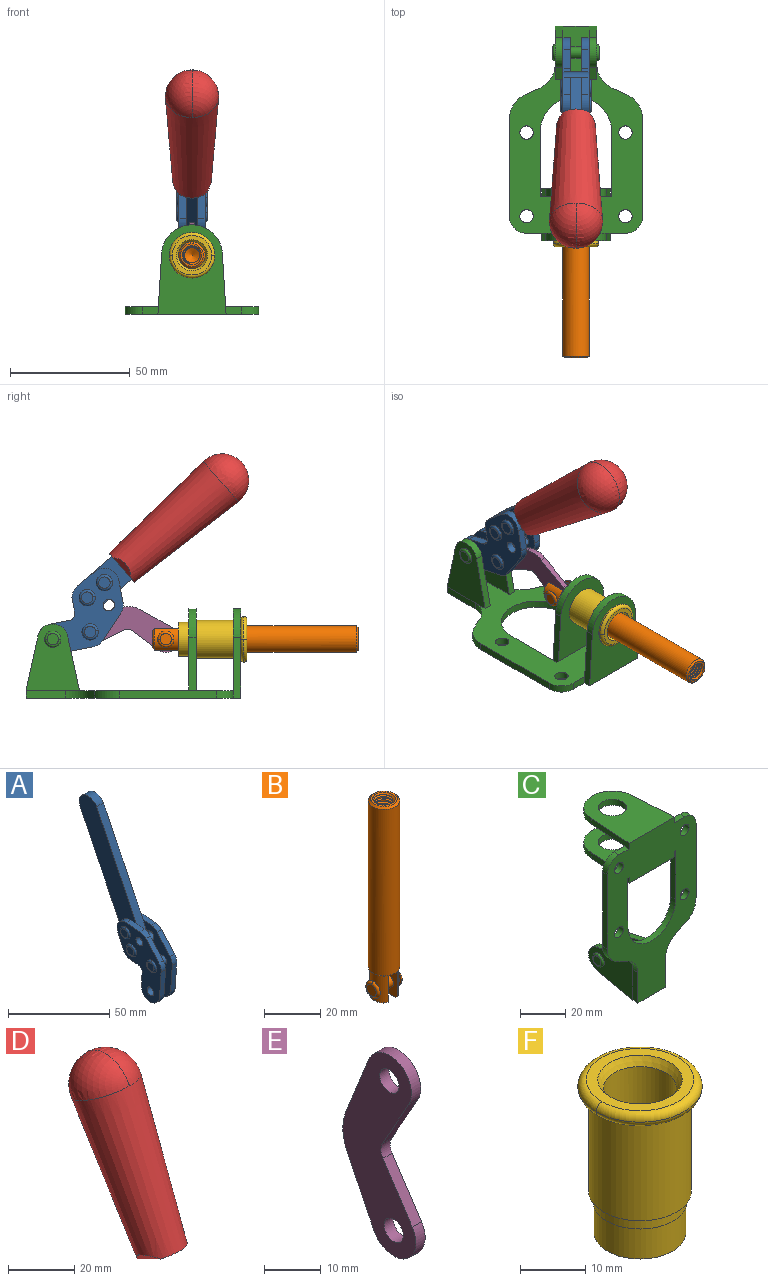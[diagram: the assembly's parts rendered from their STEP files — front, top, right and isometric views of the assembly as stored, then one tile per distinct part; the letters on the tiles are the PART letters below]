
ASSEMBLY  parts=6 mates=6
PART A: 59 faces, bbox 12.9x60.2x99.6 mm
  f0: torus R=2.39mm, axis (-1,0,0), area 14.9mm2, adj f20,f43,f51
  f1: torus R=2.39mm, axis (-1,0,0), area 14.9mm2, adj f19,f42,f51
  f2: torus R=2.39mm, axis (-1,0,0), area 14.9mm2, adj f18,f35,f51
  f3: torus R=2.39mm, axis (-1,0,0), area 14.9mm2, adj f14,f17,f23
  f4: torus R=2.39mm, axis (-1,0,0), area 14.9mm2, adj f13,f16,f23
  f5: torus R=2.39mm, axis (-1,0,0), area 14.9mm2, adj f12,f15,f23
  f6: cylinder r=2.39mm len=4.78mm, axis (1,0,0), area 46.5mm2, adj f48,f50,f51
  f7: cylinder r=2.39mm len=4.78mm, axis (1,0,0), area 46.5mm2, adj f50,f51
  f8: cylinder r=6.35mm len=12.68mm, axis (1,0,0), area 61.8mm2, adj f38,f39,f50,f51
  f9: cylinder r=2.39mm len=4.78mm, axis (-1,0,0), area 70.5mm2, adj f46,f50
  f10: cylinder r=2.39mm len=4.78mm, axis (-1,0,0), area 46.5mm2, adj f23,f45,f46
  f11: cylinder r=2.39mm len=4.78mm, axis (-1,0,0), area 46.5mm2, adj f23,f46
  f12: plane 4.78x4.78mm, normal (1,0,0), area 17.9mm2, adj f5,f15
  f13: plane 4.78x4.78mm, normal (1,0,0), area 17.9mm2, adj f4,f16
  f14: plane 4.78x4.78mm, normal (1,0,0), area 17.9mm2, adj f3,f17
  f15: torus R=2.39mm, axis (-1,0,0), area 14.9mm2, adj f5,f12,f23
  f16: torus R=2.39mm, axis (-1,0,0), area 14.9mm2, adj f4,f13,f23
  f17: torus R=2.39mm, axis (-1,0,0), area 14.9mm2, adj f3,f14,f23
  f18: plane 4.78x4.78mm, normal (-1,0,0), area 17.9mm2, adj f2,f35
  f19: plane 4.78x4.78mm, normal (-1,0,0), area 17.9mm2, adj f1,f42
  f20: plane 4.78x4.78mm, normal (-1,0,0), area 17.9mm2, adj f0,f43
  f21: plane 2.26x0.2mm, normal (1,0,0), area 0.2mm2, adj f31,f44
  f22: plane 2.26x0.2mm, normal (-1,0,0), area 0.2mm2, adj f41,f44
  f23: plane 39.37x30.77mm, normal (1,0,0), area 565.5mm2, adj f3,f4,f5,f10,f11,f15,f16,f17
  f24: cylinder r=6.1mm len=4.15mm, axis (-1,0,0), area 14.7mm2, adj f23,f25,f32,f46
  f25: plane 10.25x9.01mm, normal (0,-0.75,0.66), area 42.3mm2, adj f23,f24,f26,f46
  f26: cylinder r=6.35mm len=4.64mm, axis (-1,0,0), area 15.6mm2, adj f23,f25,f27,f46
  f27: plane 15.84x3.1mm, normal (0,-1,-0.07), area 49.2mm2, adj f23,f26,f28,f46
  f28: cylinder r=6.35mm len=12.68mm, axis (-1,0,0), area 61.8mm2, adj f23,f27,f29,f46
  f29: plane 8.11x3.1mm, normal (0,1,0.07), area 25.2mm2, adj f23,f28,f30,f46
  f30: cylinder r=3.05mm len=3.25mm, axis (-1,0,0), area 14.8mm2, adj f23,f29,f31,f46
  f31: plane 5.99x3.1mm, normal (0,0.07,-1), area 18.6mm2, adj f21,f23,f30,f44,f46
  f32: plane 9.5x3.1mm, normal (0,-0.07,1), area 29.5mm2, adj f23,f24,f33,f46,f47
  f33: cylinder r=6.1mm len=8.63mm, axis (-1,0,0), area 39.1mm2, adj f23,f32,f34,f47
  f34: plane 8.65x3.96mm, normal (0,0.91,-0.42), area 29.5mm2, adj f23,f33,f44,f47
  f35: torus R=2.39mm, axis (-1,0,0), area 14.9mm2, adj f2,f18,f51
  f36: plane 10.25x9.01mm, normal (0,-0.75,0.66), area 42.3mm2, adj f37,f49,f50,f51
  f37: cylinder r=6.35mm len=4.64mm, axis (1,0,0), area 15.6mm2, adj f36,f38,f50,f51
  f38: plane 15.84x3.1mm, normal (0,-1,-0.07), area 49.2mm2, adj f8,f37,f50,f51
  f39: plane 8.11x3.1mm, normal (0,1,0.07), area 25.2mm2, adj f8,f40,f50,f51
  f40: cylinder r=3.05mm len=3.25mm, axis (1,0,0), area 14.8mm2, adj f39,f41,f50,f51
  f41: plane 5.99x3.1mm, normal (0,0.07,-1), area 18.6mm2, adj f22,f40,f44,f50,f51
  f42: torus R=2.39mm, axis (-1,0,0), area 14.9mm2, adj f1,f19,f51
  f43: torus R=2.39mm, axis (-1,0,0), area 14.9mm2, adj f0,f20,f51
  f44: cylinder r=6.35mm len=12.12mm, axis (-1,0,0), area 128.9mm2, adj f21,f22,f23,f31,f34,f41,f46,f47
  f45: plane 2.65x1.35mm, normal (1,0,0), area 1mm2, adj f10,f55
  f46: plane 39.08x20.42mm, normal (-1,0,0), area 412.5mm2, adj f9,f10,f11,f24,f25,f26,f27,f28
  f47: plane 77.62x39.82mm, normal (1,0,0), area 850mm2, adj f32,f33,f34,f44,f53,f54,f55
  f48: plane 2.65x1.35mm, normal (-1,0,0), area 1mm2, adj f6,f55
  f49: cylinder r=6.1mm len=4.15mm, axis (1,0,0), area 14.7mm2, adj f36,f50,f51,f56
  f50: plane 39.08x20.42mm, normal (1,0,0), area 412.5mm2, adj f6,f7,f8,f9,f36,f37,f38,f39
  f51: plane 39.37x30.77mm, normal (-1,0,0), area 565.5mm2, adj f0,f1,f2,f6,f7,f8,f35,f36
  f52: plane 8.65x3.96mm, normal (0,0.91,-0.42), area 29.5mm2, adj f44,f51,f57,f58
  f53: plane 68.49x33.4mm, normal (0,0.9,-0.44), area 358.1mm2, adj f44,f47,f54,f58
  f54: cylinder r=6.35mm len=12.06mm, axis (1,0,0), area 93.7mm2, adj f47,f53,f55,f58
  f55: plane 68.49x33.4mm, normal (0,-0.9,0.44), area 358.1mm2, adj f44,f45,f46,f47,f48,f50,f54,f58
  f56: plane 9.5x3.1mm, normal (0,-0.07,1), area 29.5mm2, adj f49,f50,f51,f57,f58
  f57: cylinder r=6.1mm len=8.63mm, axis (1,0,0), area 39.1mm2, adj f51,f52,f56,f58
  f58: plane 77.62x39.82mm, normal (-1,0,0), area 850mm2, adj f44,f52,f53,f54,f55,f56,f57
PART B: 48 faces, bbox 12.6x11.1x86.1 mm
  f0: torus R=2.41mm, axis (-1,0,0), area 15mm2, adj f30,f32,f34
  f1: torus R=2.41mm, axis (-1,0,0), area 15mm2, adj f29,f31,f33
  f2: cylinder r=5.54mm len=72.39mm, axis (0,0,1), area 2518.5mm2, adj f3,f4,f42,f43
  f3: cone r=5.54mm half-angle=45deg, axis (0,0,1), area 7.6mm2, adj f2,f5,f41
  f4: cone r=5.54mm half-angle=45deg, axis (0,0,-1), area 34.9mm2, adj f2,f39
  f5: cylinder r=5.08mm len=11.48mm, axis (0,0,1), area 108.3mm2, adj f3,f7,f8,f41
  f6: cylinder r=2.41mm len=4.83mm, axis (-1,0,0), area 71.2mm2, adj f40,f41
  f7: cylinder r=2.41mm len=4.83mm, axis (-1,0,0), area 7.6mm2, adj f5,f34
  f8: cone r=5.08mm half-angle=45deg, axis (0,0,1), area 10.6mm2, adj f5,f37,f41
  f9: cone r=3.98mm half-angle=45deg, axis (0,0,1), area 17.6mm2, adj f27,f39,f45,f46,f47
  f10: cylinder r=2.41mm len=4.83mm, axis (-1,0,0), area 7.6mm2, adj f33,f38
  f11: cylinder r=3.2mm len=6.4mm, axis (0,0,1), area 78.4mm2, adj f12,f28,f44,f45,f47
  f12: cylinder r=3.2mm len=6.4mm, axis (0,0,1), area 10.5mm2, adj f11,f13,f45,f47
  f13: cylinder r=3.2mm len=6.4mm, axis (0,0,1), area 10.5mm2, adj f12,f14,f45,f47
  f14: cylinder r=3.2mm len=6.4mm, axis (0,0,1), area 10.5mm2, adj f13,f15,f45,f47
  f15: cylinder r=3.2mm len=6.4mm, axis (0,0,1), area 10.5mm2, adj f14,f16,f45,f47
  f16: cylinder r=3.2mm len=6.4mm, axis (0,0,1), area 10.5mm2, adj f15,f17,f45,f47
  f17: cylinder r=3.2mm len=6.4mm, axis (0,0,1), area 10.5mm2, adj f16,f18,f45,f47
  f18: cylinder r=3.2mm len=6.4mm, axis (0,0,1), area 10.5mm2, adj f17,f19,f45,f47
  f19: cylinder r=3.2mm len=6.4mm, axis (0,0,1), area 10.5mm2, adj f18,f20,f45,f47
  f20: cylinder r=3.2mm len=6.4mm, axis (0,0,1), area 10.5mm2, adj f19,f21,f45,f47
  f21: cylinder r=3.2mm len=6.4mm, axis (0,0,1), area 10.5mm2, adj f20,f22,f45,f47
  f22: cylinder r=3.2mm len=6.4mm, axis (0,0,1), area 10.5mm2, adj f21,f23,f45,f47
  f23: cylinder r=3.2mm len=6.4mm, axis (0,0,1), area 10.5mm2, adj f22,f24,f45,f47
  f24: cylinder r=3.2mm len=6.4mm, axis (0,0,1), area 10.5mm2, adj f23,f25,f45,f47
  f25: cylinder r=3.2mm len=6.4mm, axis (0,0,1), area 10.5mm2, adj f24,f26,f45,f47
  f26: cylinder r=3.2mm len=6.4mm, axis (0,0,1), area 10.5mm2, adj f25,f27,f45,f47
  f27: cylinder r=3.2mm len=6.4mm, axis (0,0,1), area 7.4mm2, adj f9,f26,f45,f47
  f28: cone r=3.2mm half-angle=60deg, axis (0,0,1), area 37.2mm2, adj f11
  f29: plane 4.83x4.83mm, normal (-1,0,0), area 18.3mm2, adj f1,f31
  f30: plane 4.83x4.83mm, normal (1,0,0), area 18.3mm2, adj f0,f32
  f31: torus R=2.41mm, axis (-1,0,0), area 15mm2, adj f1,f29,f33
  f32: torus R=2.41mm, axis (-1,0,0), area 15mm2, adj f0,f30,f34
  f33: plane 6.83x6.83mm, normal (1,0,0), area 18.3mm2, adj f1,f10,f31
  f34: plane 6.83x6.83mm, normal (-1,0,0), area 18.3mm2, adj f0,f7,f32
  f35: cone r=5.08mm half-angle=45deg, axis (0,0,1), area 10.6mm2, adj f36,f38,f40
  f36: plane 7.25x1.97mm, normal (0,0,-1), area 10mm2, adj f35,f40
  f37: plane 7.25x1.97mm, normal (0,0,-1), area 10mm2, adj f8,f41
  f38: cylinder r=5.08mm len=11.48mm, axis (0,0,1), area 108.3mm2, adj f10,f35,f40,f42
  f39: plane 9.55x9.55mm, normal (0,0,1), area 22mm2, adj f4,f9
  f40: plane 12.76x10.09mm, normal (1,0,0), area 95.7mm2, adj f6,f35,f36,f38,f42,f43
  f41: plane 12.76x10.09mm, normal (-1,0,0), area 95.7mm2, adj f3,f5,f6,f8,f37,f43
  f42: cone r=5.54mm half-angle=45deg, axis (0,0,1), area 7.6mm2, adj f2,f38,f40
  f43: plane 11.07x4.7mm, normal (0,0,-1), area 50.4mm2, adj f2,f40,f41
  f44: plane 0.89x0.62mm, normal (-1,0,0), area 0.3mm2, adj f11,f45,f46,f47
  f45: bspline ~24.8x7.63mm, area 266.6mm2, adj f9,f11,f12,f13,f14,f15,f16,f17
  f46: bspline ~24.87x7.63mm, area 73.6mm2, adj f9,f44,f45,f47
  f47: bspline ~24.98x7.63mm, area 272.5mm2, adj f9,f11,f12,f13,f14,f15,f16,f17
PART C: 55 faces, bbox 55.7x37.4x89.8 mm
  f0: torus R=2.41mm, axis (-1,0,0), area 15mm2, adj f11,f15,f25
  f1: torus R=2.41mm, axis (-1,0,0), area 15mm2, adj f10,f12,f22
  f2: cylinder r=2.78mm len=5.56mm, axis (0,-1,0), area 54.2mm2, adj f30,f54
  f3: cylinder r=14.99mm len=29.97mm, axis (0,-1,0), area 145.9mm2, adj f30,f49,f53,f54
  f4: cylinder r=2.78mm len=5.56mm, axis (0,-1,0), area 54.2mm2, adj f30,f54
  f5: cylinder r=2.78mm len=5.56mm, axis (0,-1,0), area 54.2mm2, adj f30,f54
  f6: cylinder r=2.78mm len=5.56mm, axis (0,-1,0), area 54.2mm2, adj f30,f54
  f7: cylinder r=6.35mm len=12.7mm, axis (0,0,1), area 123.6mm2, adj f27,f51
  f8: cylinder r=6.35mm len=12.7mm, axis (0,0,-1), area 124.7mm2, adj f21,f35
  f9: cylinder r=2.41mm len=11.18mm, axis (-1,0,0), area 169.4mm2, adj f16,f19
  f10: plane 4.83x4.83mm, normal (1,0,0), area 18.3mm2, adj f1,f12
  f11: plane 4.83x4.83mm, normal (-1,0,0), area 18.3mm2, adj f0,f15
  f12: torus R=2.41mm, axis (-1,0,0), area 15mm2, adj f1,f10,f22
  f13: cylinder r=6.35mm len=12.41mm, axis (1,0,0), area 53.4mm2, adj f18,f19,f22,f23
  f14: cylinder r=6.35mm len=12.41mm, axis (-1,0,0), area 53.4mm2, adj f16,f17,f24,f25
  f15: torus R=2.41mm, axis (-1,0,0), area 15mm2, adj f0,f11,f25
  f16: plane 27.86x22.35mm, normal (1,0,0), area 425.4mm2, adj f9,f14,f17,f24,f30
  f17: plane 22.86x4.97mm, normal (0,0.21,0.98), area 72.5mm2, adj f14,f16,f25,f30
  f18: plane 22.86x4.97mm, normal (0,0.21,0.98), area 72.5mm2, adj f13,f19,f22,f30
  f19: plane 27.86x22.35mm, normal (-1,0,0), area 425.4mm2, adj f9,f13,f18,f23,f30
  f20: cylinder r=12.7mm len=25.35mm, axis (0,0,-1), area 119.8mm2, adj f21,f34,f35,f36
  f21: plane 34.21x28.07mm, normal (0,0,-1), area 702.4mm2, adj f8,f20,f30,f34,f36
  f22: plane 27.96x22.45mm, normal (1,0,0), area 407.2mm2, adj f1,f12,f13,f18,f23,f30,f42,f43
  f23: plane 22.86x4.97mm, normal (0,0.21,-0.98), area 72.5mm2, adj f13,f19,f22,f44
  f24: plane 22.86x4.97mm, normal (0,0.21,-0.98), area 72.5mm2, adj f14,f16,f25,f44
  f25: plane 27.86x22.35mm, normal (-1,0,0), area 407.1mm2, adj f0,f14,f15,f17,f24,f30,f45,f46
  f26: plane 3.1x0.95mm, normal (0,0,-1), area 2.7mm2, adj f30,f49,f50,f54
  f27: plane 34.21x28.07mm, normal (0,0,1), area 702.4mm2, adj f7,f28,f30,f50,f52
  f28: cylinder r=12.7mm len=25.35mm, axis (0,0,1), area 118.8mm2, adj f27,f50,f51,f52
  f29: plane 3.1x0.95mm, normal (0,0,-1), area 2.7mm2, adj f30,f52,f53,f54
  f30: plane 86.54x55.63mm, normal (0,1,0), area 2362.9mm2, adj f2,f3,f4,f5,f6,f16,f17,f18
  f31: plane 40.56x3.1mm, normal (-1,0,0), area 125.7mm2, adj f30,f32,f48,f54
  f32: cylinder r=7.11mm len=7.11mm, axis (0,-1,0), area 34.6mm2, adj f30,f31,f33,f54
  f33: plane 6.67x3.1mm, normal (0,0,1), area 20.4mm2, adj f30,f32,f34,f54
  f34: plane 25.39x3.13mm, normal (-1,0.06,0), area 79.5mm2, adj f20,f21,f33,f35,f54
  f35: plane 37.31x28.45mm, normal (0,0,1), area 789.9mm2, adj f8,f20,f34,f36,f54
  f36: plane 25.39x3.13mm, normal (1,0.06,0), area 79.5mm2, adj f20,f21,f35,f37,f54
  f37: plane 6.67x3.1mm, normal (0,0,1), area 20.4mm2, adj f30,f36,f38,f54
  f38: cylinder r=7.11mm len=7.11mm, axis (0,-1,0), area 34.6mm2, adj f30,f37,f39,f54
  f39: plane 40.56x3.1mm, normal (1,0,0), area 125.7mm2, adj f30,f38,f40,f54
  f40: cylinder r=11.18mm len=10.16mm, axis (0,-1,0), area 39.5mm2, adj f30,f39,f41,f54
  f41: plane 6.09x3.1mm, normal (0.42,0,-0.91), area 20.8mm2, adj f30,f40,f42,f54
  f42: cylinder r=11.18mm len=9.41mm, axis (0,-1,0), area 37.2mm2, adj f22,f30,f41,f43,f54
  f43: plane 16.5x3.1mm, normal (1,0,0), area 51.1mm2, adj f22,f42,f44,f54
  f44: plane 17.37x3.1mm, normal (0,0,-1), area 53.8mm2, adj f23,f24,f30,f43,f45,f54
  f45: plane 16.5x3.1mm, normal (-1,0,0), area 51.1mm2, adj f25,f44,f46,f54
  f46: cylinder r=11.18mm len=9.41mm, axis (0,-1,0), area 37.2mm2, adj f25,f30,f45,f47,f54
  f47: plane 6.09x3.1mm, normal (-0.42,0,-0.91), area 20.8mm2, adj f30,f46,f48,f54
  f48: cylinder r=11.18mm len=10.16mm, axis (0,-1,0), area 39.5mm2, adj f30,f31,f47,f54
  f49: plane 26.54x3.1mm, normal (-1,0,0), area 82.3mm2, adj f3,f26,f30,f54
  f50: plane 25.39x3.1mm, normal (1,0.06,0), area 78.8mm2, adj f26,f27,f28,f51,f54
  f51: plane 37.31x28.45mm, normal (0,0,-1), area 789.9mm2, adj f7,f28,f50,f52,f54
  f52: plane 25.39x3.1mm, normal (-1,0.06,0), area 78.8mm2, adj f27,f28,f29,f51,f54
  f53: plane 26.54x3.1mm, normal (1,0,0), area 82.3mm2, adj f3,f29,f30,f54
  f54: plane 89.66x55.63mm, normal (0,-1,0), area 2678.5mm2, adj f2,f3,f4,f5,f6,f26,f29,f31
PART D: 11 faces, bbox 22.3x42.6x64.5 mm
  f0: sphere r=11.13mm, area 411.4mm2, adj f1,f8
  f1: cone r=11.11mm half-angle=3.3deg, axis (0,0.44,0.9), area 3251.8mm2, adj f0,f7,f8,f9,f10
  f2: cylinder r=6.16mm len=11.7mm, axis (1,0,0), area 89.5mm2, adj f3,f4,f5,f6
  f3: plane 60.23x36.75mm, normal (-1,0,0), area 763.6mm2, adj f2,f4,f6,f10
  f4: plane 51.37x25.05mm, normal (0,0.9,-0.44), area 264.2mm2, adj f2,f3,f5,f10
  f5: plane 60.23x36.75mm, normal (1,0,0), area 763.6mm2, adj f2,f4,f6,f10
  f6: plane 51.37x25.05mm, normal (0,-0.9,0.44), area 264.2mm2, adj f2,f3,f5,f10
  f7: plane 9.95x5.95mm, normal (0.71,-0.31,-0.64), area 25.8mm2, adj f1,f10
  f8: sphere r=11.13mm, area 411.4mm2, adj f0,f1
  f9: plane 9.95x5.95mm, normal (-0.71,-0.31,-0.64), area 25.8mm2, adj f1,f10
  f10: plane 14.27x11.38mm, normal (0,-0.44,-0.9), area 106.7mm2, adj f1,f3,f4,f5,f6,f7,f9
PART E: 12 faces, bbox 2.3x18.2x42.8 mm
  f0: cylinder r=2.4mm len=4.8mm, axis (1,0,0), area 34.9mm2, adj f4,f11
  f1: cylinder r=10.41mm len=8.47mm, axis (1,0,0), area 20.2mm2, adj f4,f9,f10,f11
  f2: cylinder r=3.05mm len=3.16mm, axis (1,0,0), area 7.7mm2, adj f4,f6,f7,f11
  f3: cylinder r=2.4mm len=4.8mm, axis (1,0,0), area 34.9mm2, adj f4,f11
  f4: plane 42.81x18.23mm, normal (-1,0,0), area 414.1mm2, adj f0,f1,f2,f3,f5,f6,f7,f8
  f5: cylinder r=5.54mm len=10.67mm, axis (1,0,0), area 41.8mm2, adj f4,f6,f10,f11
  f6: plane 11.66x6.53mm, normal (0,-0.87,-0.49), area 30.9mm2, adj f2,f4,f5,f11
  f7: plane 11.17x7.33mm, normal (0,-0.84,0.55), area 30.9mm2, adj f2,f4,f8,f11
  f8: cylinder r=5.54mm len=10.51mm, axis (1,0,0), area 41.8mm2, adj f4,f7,f9,f11
  f9: plane 13.67x6.67mm, normal (0,0.9,-0.44), area 35.1mm2, adj f1,f4,f8,f11
  f10: plane 14.1x5.7mm, normal (0,0.93,0.37), area 35.1mm2, adj f1,f4,f5,f11
  f11: plane 42.81x18.23mm, normal (1,0,0), area 414.1mm2, adj f0,f1,f2,f3,f5,f6,f7,f8
PART F: 15 faces, bbox 20.6x20.6x28.7 mm
  f0: torus R=8.26mm, axis (0,0,1), area 56.8mm2, adj f1,f10,f12
  f1: torus R=8.26mm, axis (0,0,1), area 56.8mm2, adj f0,f6,f13
  f2: cylinder r=5.59mm len=25.91mm, axis (0,0,1), area 909.6mm2, adj f3,f4
  f3: cone r=6.86mm half-angle=45deg, axis (0,0,-1), area 70.2mm2, adj f2,f14
  f4: cone r=6.47mm half-angle=30deg, axis (0,0,1), area 66.7mm2, adj f2,f13
  f5: cylinder r=7.04mm len=14.07mm, axis (0,0,1), area 252.6mm2, adj f11,f14
  f6: torus R=8.26mm, axis (0,0,1), area 56.8mm2, adj f1,f12,f13
  f7: cylinder r=7.16mm len=14.33mm, axis (0,0,1), area 91.5mm2, adj f9,f11
  f8: cylinder r=7.86mm len=18.42mm, axis (0,0,1), area 909.6mm2, adj f9,f10
  f9: plane 15.72x15.72mm, normal (0,0,-1), area 33mm2, adj f7,f8
  f10: plane 16.51x16.51mm, normal (0,0,-1), area 19.9mm2, adj f0,f8,f12
  f11: plane 14.33x14.33mm, normal (0,0,-1), area 5.7mm2, adj f5,f7
  f12: torus R=8.26mm, axis (0,0,1), area 56.8mm2, adj f0,f6,f10
  f13: plane 16.51x16.51mm, normal (0,0,1), area 82.7mm2, adj f1,f4,f6
  f14: plane 14.07x14.07mm, normal (0,0,-1), area 7.8mm2, adj f3,f5
PLACE A rot(axis=(1,0,0),75deg) t=(0,3.86,9.14)mm
PLACE B rot(axis=(1,0,0),90deg) t=(0,9.52,0)mm
PLACE C rot(axis=(1,0,0),90deg) t=(0,9.14,0)mm fixed
PLACE D rot(axis=(1,0,0),75deg) t=(0,3.86,9.14)mm
PLACE E rot(axis=(1,0,0),97.5deg) t=(0,12.59,2.22)mm
PLACE F rot(axis=(1,0,0),90deg) t=(0,9.14,0)mm
MATE fastened D.f2 <-> A.f54  axis (1,0,0) through (0,-30.66,91.94)mm
MATE revolute B.f6 <-> E.f5  axis (-1,0,0) through (0,-5.96,24.61)mm
MATE revolute E.f3 <-> A.f4  axis (1,0,0) through (0,25.65,27.64)mm
MATE fastened C.f7 <-> F.f0  axis (0,-1,0) through (0,-37.25,24.61)mm
MATE slider B.f2 <-> C.f7  axis (0,-1,0) through (0,-49.26,24.61)mm
MATE revolute A.f7 <-> C.f0  axis (1,0,0) through (0,41.23,24.61)mm
